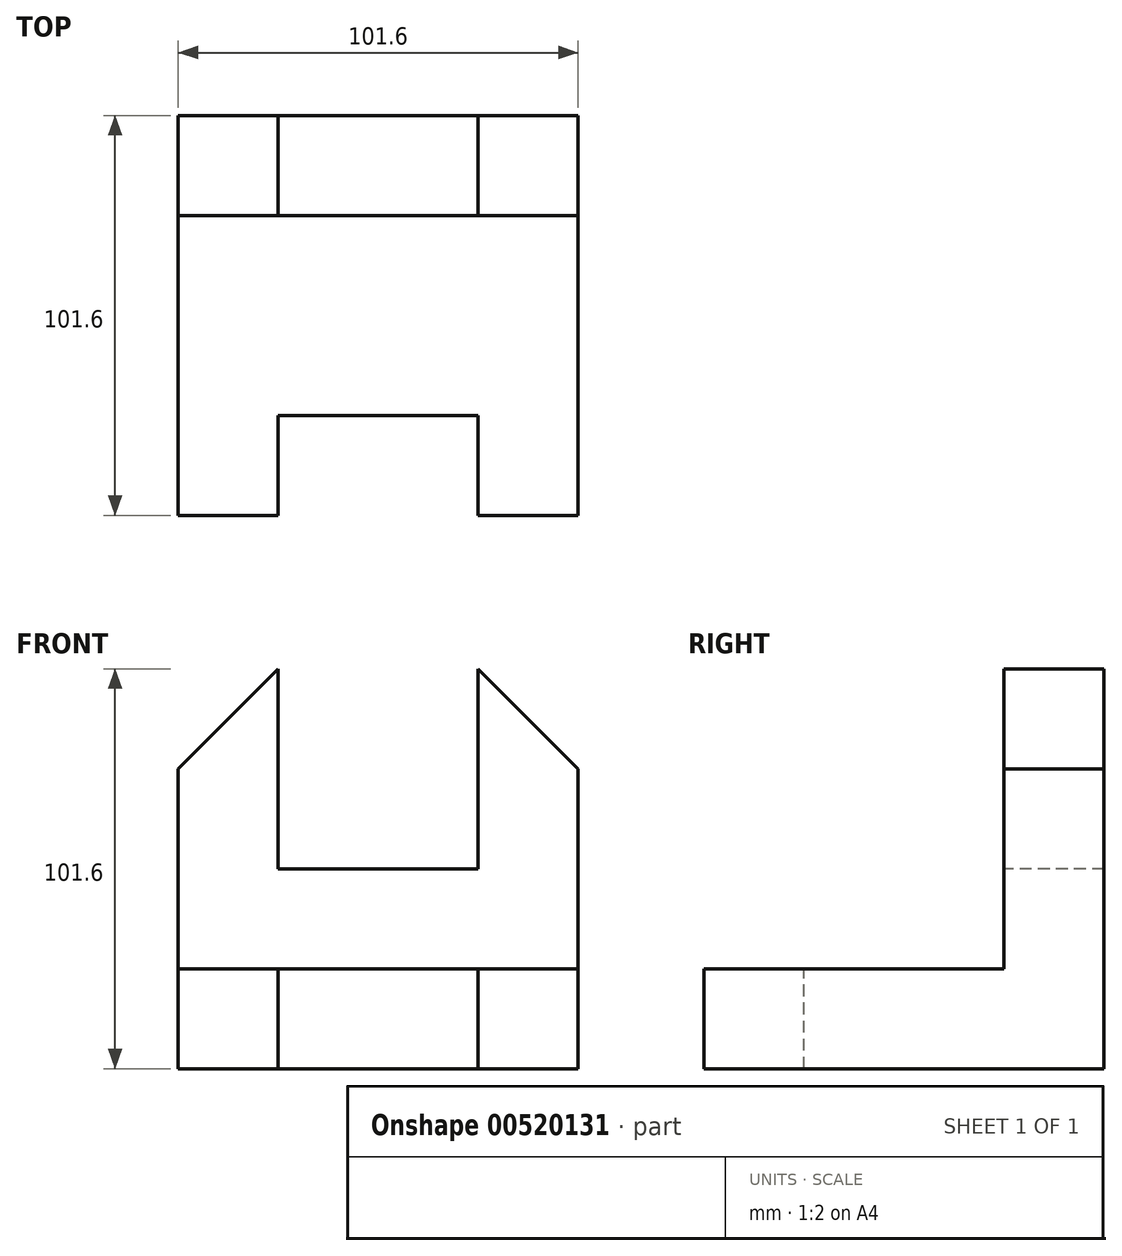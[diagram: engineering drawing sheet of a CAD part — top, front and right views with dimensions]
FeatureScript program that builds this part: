
annotation { "Feature Type Name" : "Feature", "Feature Type Description" : "" }
export const myFeature = defineFeature(function(context is Context, id is Id, definition is map)
    precondition{}
    {
        {
            var Q0;
            Q0=qCreatedBy(makeId("Right.planeOp"),FACE);
            var sketch = newSketch(context, id + "F0", { "sketchPlane" : qUnion([Q0])});
            skLineSegment(sketch, "E0.bottom", {"start": v(0, 0) * mm, "end": v(-101.6, 0) * mm});
            skLineSegment(sketch, "E0.top", {"start": v(0, 101.6) * mm, "end": v(-101.6, 101.6) * mm});
            skLineSegment(sketch, "E0.left", {"start": v(0, 0) * mm, "end": v(0, 101.6) * mm});
            skLineSegment(sketch, "E0.right", {"start": v(-101.6, 0) * mm, "end": v(-101.6, 101.6) * mm});
            skSolve(sketch);
        }
        {
            var Q0;
            Q0=makeQuery(id+"F0.imprint","IMPRINT",FACE,{"disambiguationData":[TD([[makeQuery(id+"F0.imprint","IMPRINT",EDGE,{"derivedFrom":sQuery(id+"F0.wireOp",EDGE,"E0.bottom")}),-1.0]])]});
            extrude(context, id + "F1", {"entities" : qUnion([Q0]), "depth" : 101.6 * mm, "offsetDistance" : 25.4 * mm});
        }
        {
            var Q0;
            Q0=makeQuery(id+"F1.opExtrude","CAP_FACE",FACE,{"disambiguationData":[OSD([sQuery(id+"F0.wireOp",EDGE,"E0.bottom"),sQuery(id+"F0.wireOp",EDGE,"E0.top"),sQuery(id+"F0.wireOp",EDGE,"E0.left"),sQuery(id+"F0.wireOp",EDGE,"E0.right")])],"isStart":false});
            var sketch = newSketch(context, id + "F2", { "sketchPlane" : qUnion([Q0])});
            skLineSegment(sketch, "E1", {"start": v(-101.6, 0) * mm, "end": v(-101.6, 25.4) * mm});
            skLineSegment(sketch, "E2", {"start": v(-101.6, 25.4) * mm, "end": v(-25.4, 25.4) * mm});
            skLineSegment(sketch, "E3", {"start": v(-25.4, 25.4) * mm, "end": v(-25.4, 101.6) * mm});
            skSolve(sketch);
        }
        {
            var Q0;
            {var subQ0=sQuery(id+"F2.wireOp",EDGE,"E2");Q0=makeQuery(id+"F2.imprint","IMPRINT",FACE,{"disambiguationData":[TD([[makeQuery(id+"F2.imprint","IMPRINT",EDGE,{"derivedFrom":subQ0}),1.0]])]});}
            extrude(context, id + "F3", {"entities" : qUnion([Q0]), "operationType" : NewBodyOperationType.REMOVE, "oppositeDirection" : true, "depth" : 160.78 * mm, "offsetDistance" : 25.4 * mm});
        }
        {
            var Q0;
            Q0=makeQuery(id+"F3.boolean.opBoolean","COPY",FACE,{"derivedFrom":makeQuery(id+"F3.opExtrude","SWEPT_FACE",FACE,{"disambiguationData":[OSD([sQuery(id+"F2.wireOp",EDGE,"E2")])]})});
            var sketch = newSketch(context, id + "F4", { "sketchPlane" : qUnion([Q0])});
            skLineSegment(sketch, "E4", {"start": v(0, -101.6) * mm, "end": v(25.4, -101.6) * mm});
            skLineSegment(sketch, "E5", {"start": v(25.4, -101.6) * mm, "end": v(25.4, -76.2) * mm});
            skLineSegment(sketch, "E6", {"start": v(25.4, -76.2) * mm, "end": v(76.2, -76.2) * mm});
            skLineSegment(sketch, "E7", {"start": v(76.2, -76.2) * mm, "end": v(76.2, -101.6) * mm});
            skLineSegment(sketch, "E8", {"start": v(76.2, -101.6) * mm, "end": v(25.4, -101.6) * mm});
            skSolve(sketch);
        }
        {
            var Q0;
            Q0=makeQuery(id+"F3.boolean.opBoolean","COPY",FACE,{"derivedFrom":makeQuery(id+"F3.opExtrude","SWEPT_FACE",FACE,{"disambiguationData":[OSD([sQuery(id+"F2.wireOp",EDGE,"E3")])]})});
            var sketch = newSketch(context, id + "F5", { "sketchPlane" : qUnion([Q0])});
            skLineSegment(sketch, "E9", {"start": v(0, 101.6) * mm, "end": v(25.4, 101.6) * mm});
            skLineSegment(sketch, "E10", {"start": v(25.4, 101.6) * mm, "end": v(25.4, 50.8) * mm});
            skLineSegment(sketch, "E11", {"start": v(25.4, 50.8) * mm, "end": v(76.2, 50.8) * mm});
            skLineSegment(sketch, "E12", {"start": v(76.2, 50.8) * mm, "end": v(76.2, 101.6) * mm});
            skLineSegment(sketch, "E13", {"start": v(76.2, 101.6) * mm, "end": v(25.4, 101.6) * mm});
            skLineSegment(sketch, "E14", {"start": v(25.4, 101.6) * mm, "end": v(0, 101.6) * mm});
            skLineSegment(sketch, "E15", {"start": v(0, 101.6) * mm, "end": v(0, 76.2) * mm});
            skLineSegment(sketch, "E16", {"start": v(0, 76.2) * mm, "end": v(25.4, 76.2) * mm});
            skLineSegment(sketch, "E17", {"start": v(76.2, 101.6) * mm, "end": v(101.6, 101.6) * mm});
            skLineSegment(sketch, "E18", {"start": v(101.6, 101.6) * mm, "end": v(101.6, 76.2) * mm});
            skLineSegment(sketch, "E19", {"start": v(101.6, 76.2) * mm, "end": v(76.2, 76.2) * mm});
            skLineSegment(sketch, "E20", {"start": v(76.2, 76.2) * mm, "end": v(76.2, 101.6) * mm});
            skSolve(sketch);
        }
        {
            var Q0;
            {var subQ0=sQuery(id+"F5.wireOp",EDGE,"E11");Q0=makeQuery(id+"F5.imprint","IMPRINT",FACE,{"disambiguationData":[TD([[makeQuery(id+"F5.imprint","IMPRINT",EDGE,{"derivedFrom":subQ0}),1.0]])]});}
            extrude(context, id + "F6", {"entities" : qUnion([Q0]), "operationType" : NewBodyOperationType.REMOVE, "oppositeDirection" : true, "depth" : 60.2 * mm, "offsetDistance" : 25.4 * mm});
        }
        {
            var Q0;
            Q0=makeQuery(id+"F3.boolean.opBoolean","COPY",FACE,{"derivedFrom":makeQuery(id+"F3.opExtrude","SWEPT_FACE",FACE,{"disambiguationData":[OSD([sQuery(id+"F2.wireOp",EDGE,"E3")])]})});
            var sketch = newSketch(context, id + "F7", { "sketchPlane" : qUnion([Q0])});
            skLineSegment(sketch, "E21", {"start": v(25.4, 101.6) * mm, "end": v(25.4, 76.2) * mm});
            skLineSegment(sketch, "E22", {"start": v(25.4, 76.2) * mm, "end": v(0, 76.2) * mm});
            skLineSegment(sketch, "E23", {"start": v(0, 76.2) * mm, "end": v(0, 101.6) * mm});
            skLineSegment(sketch, "E24", {"start": v(0, 101.6) * mm, "end": v(25.4, 101.6) * mm});
            skLineSegment(sketch, "E25", {"start": v(76.2, 101.6) * mm, "end": v(101.6, 101.6) * mm});
            skLineSegment(sketch, "E26", {"start": v(101.6, 101.6) * mm, "end": v(101.6, 76.2) * mm});
            skLineSegment(sketch, "E27", {"start": v(101.6, 76.2) * mm, "end": v(76.2, 76.2) * mm});
            skLineSegment(sketch, "E28", {"start": v(76.2, 76.2) * mm, "end": v(76.2, 101.6) * mm});
            skLineSegment(sketch, "E29", {"start": v(101.6, 101.6) * mm, "end": v(76.2, 101.6) * mm});
            skLineSegment(sketch, "E30", {"start": v(76.2, 101.6) * mm, "end": v(101.6, 76.2) * mm});
            skLineSegment(sketch, "E31", {"start": v(25.4, 101.6) * mm, "end": v(0, 76.2) * mm});
            skSolve(sketch);
        }
        {
            var Q0;
            Q0=makeQuery(id+"F7.imprint","IMPRINT",FACE,{"disambiguationData":[TD([[makeQuery(id+"F7.imprint","IMPRINT",EDGE,{"derivedFrom":sQuery(id+"F7.wireOp",EDGE,"E26")}),1.0]])]});
            var Q1;
            Q1=makeQuery(id+"F7.imprint","IMPRINT",FACE,{"disambiguationData":[TD([[makeQuery(id+"F7.imprint","IMPRINT",EDGE,{"derivedFrom":sQuery(id+"F7.wireOp",EDGE,"E23")}),-1.0]])]});
            extrude(context, id + "F8", {"entities" : qUnion([Q0, Q1]), "operationType" : NewBodyOperationType.REMOVE, "oppositeDirection" : true, "depth" : 66.8 * mm, "offsetDistance" : 25.4 * mm});
        }
        {
            var Q0;
            Q0=makeQuery(id+"F4.imprint","IMPRINT",FACE,{"disambiguationData":[TD([[makeQuery(id+"F4.imprint","IMPRINT",EDGE,{"derivedFrom":sQuery(id+"F4.wireOp",EDGE,"E5")}),-1.0]])]});
            extrude(context, id + "F9", {"entities" : qUnion([Q0]), "operationType" : NewBodyOperationType.REMOVE, "oppositeDirection" : true, "depth" : 78.49 * mm, "offsetDistance" : 25.4 * mm});
        }
    });
